# Revit family: VTp759 Отвод45
name_source: partatom
category: Соединительные детали трубопроводов
revit_build: Autodesk Revit 2015 (Build: 20140606_1530(x64)
units: mm (PartAtom-declared; Revit-internal decimal feet)

## types (6) — shared parameters
Группа модели = VTp.700
Изготовитель = VALTEC S.R.L.
Коэффициент K = 0.5
Метод определения потерь = Коэффициент K
Описание = Отвод 45
Таблица коэффициентов K = Angle Valve Threaded

## per-type parameters (varying)
| type | 20 | 25 | 32 | 40 | 50 | 63 | A | B | d | Код по классификатору |
| 20 | Да | Нет | Нет | Нет | Нет | Нет | 21 мм | 15 мм | 20 мм | VTp.759.0.020 |
| 25 | Нет | Да | Нет | Нет | Нет | Нет | 24 мм | 17 мм | 25 мм | VTp.759.0.025 |
| 40 | Нет | Нет | Нет | Да | Нет | Нет | 35 мм | 21 мм | 40 мм | VTp.759.0.040 |
| 32 | Нет | Нет | Да | Нет | Нет | Нет | 28 мм | 18 мм | 32 мм | VTp.759.0.032 |
| 50 | Нет | Нет | Нет | Нет | Да | Нет | 40 мм | 24 мм | 50 мм | VTp.759.0.050 |
| 63 | Нет | Нет | Нет | Нет | Нет | Да | 68 мм | 26 мм | 63 мм | VTp.759.0.063 |
